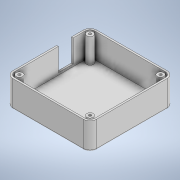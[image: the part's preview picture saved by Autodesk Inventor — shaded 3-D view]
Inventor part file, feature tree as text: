
AUTODESK INVENTOR PART (.ipt)
format: ipt  version: 2020 (Build 240168000, 168)  size: 163,328 bytes
history: native  units: in
note: dims shown in document units (in); Inventor stores cm internally (conversion verified against a paired STEP export)
features: extrude x3, sketch x3, mirror x2, shell x1, fillet x1
ambient origin geometry x8: Origin, YZ Plane, XZ Plane, XY Plane, X Axis, Y Axis, Z Axis, Center Point
bodies: Solid1 (feature_tree)
feature tree (10):
  extrude  "Extrusion1"  Depth=3.1496in
  shell  "Shell1"  Thickness=0.25in
  fillet  "Fillet1"  Radius=1.0in
  extrude  "Extrusion2"  Depth=0.05in
  mirror  "Mirror1"
  mirror  "Mirror2"
  extrude  "Extrusion3"  Depth=1.0in
  sketch  "Sketch1"  dims[d0=3.1496in d1=3.1496in d2=0.25in d3=1.0in d4=0.0in]
  sketch  "Sketch2"  dims[d5=0.0669in d6=0.05in]
  sketch  "Sketch3"  dims[d7=0.25in d8=0.0945in d9=1.0in d10=0.0in d11=0.5512in d12=0.85in d13=0.7in d14=1.0in d15=0.0in]
